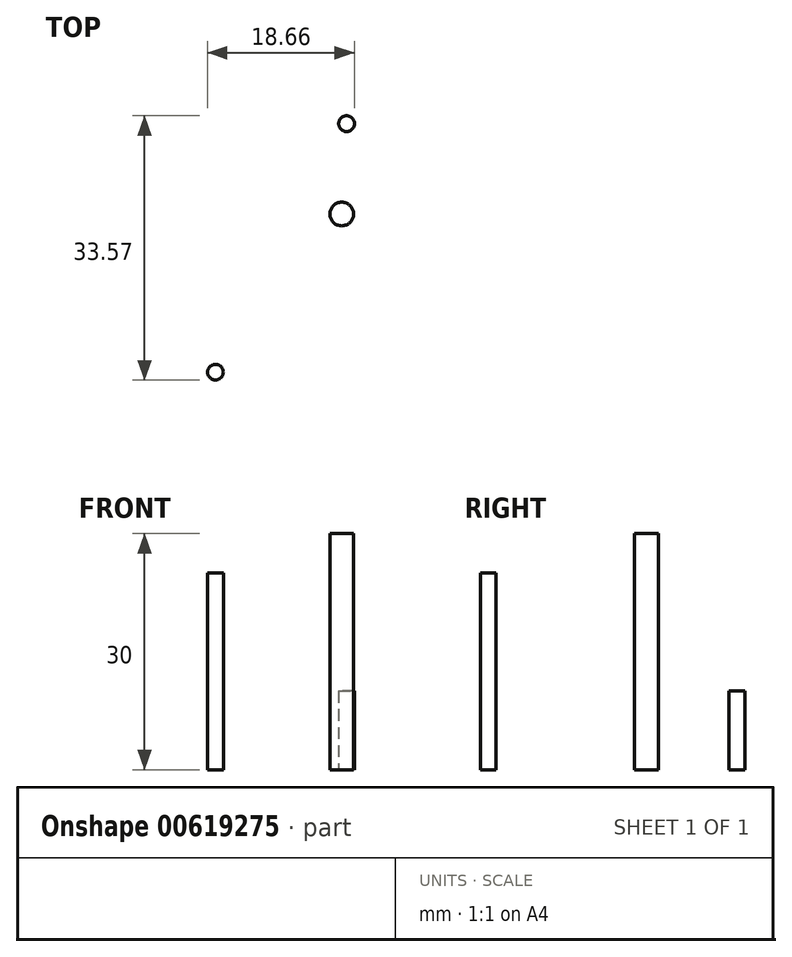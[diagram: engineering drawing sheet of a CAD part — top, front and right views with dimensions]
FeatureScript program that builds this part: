
annotation { "Feature Type Name" : "Feature", "Feature Type Description" : "" }
export const myFeature = defineFeature(function(context is Context, id is Id, definition is map)
    precondition{}
    {
        {
            var Q0;
            Q0=qCreatedBy(makeId("Top.planeOp"),FACE);
            var sketch = newSketch(context, id + "F0", { "sketchPlane" : qUnion([Q0])});
            skCircle(sketch, "E0", {"center": v(26.42, 32.5) * mm, "radius": 1 * mm});
            skSolve(sketch);
        }
        {
            var Q0;
            Q0=makeQuery(id+"F0.imprint","IMPRINT",FACE,{"disambiguationData":[TD([[makeQuery(id+"F0.imprint","IMPRINT",EDGE,{"derivedFrom":sQuery(id+"F0.wireOp",EDGE,"HmnpBGPK-XCcR-qBLW-umx0-wRZoGpGYpxc2")}),1.0]])]});
            var Q1;
            Q1=makeQuery(id+"F0.imprint","IMPRINT",FACE,{"disambiguationData":[TD([[makeQuery(id+"F0.imprint","IMPRINT",EDGE,{"derivedFrom":sQuery(id+"F0.wireOp",EDGE,"E0")}),1.0]])]});
            var Q2;
            Q2=makeQuery(id+"F0.imprint","IMPRINT",FACE,{"disambiguationData":[TD([[makeQuery(id+"F0.imprint","IMPRINT",EDGE,{"derivedFrom":sQuery(id+"F0.wireOp",EDGE,"ZV8fRuly-QuCs-XrdZ-uMXn-ZUZRQThLSaRu")}),-1.0]])]});
            extrude(context, id + "F1", {"entities" : qUnion([Q0, Q1, Q2]), "depth" : 25 * mm, "offsetDistance" : 25 * mm});
        }
        {
            var Q0;
            Q0=qCreatedBy(makeId("Top.planeOp"),FACE);
            var sketch = newSketch(context, id + "F2", { "sketchPlane" : qUnion([Q0])});
            skCircle(sketch, "E1", {"center": v(43.08, 64.08) * mm, "radius": 1 * mm});
            skSolve(sketch);
        }
        {
            var Q0;
            Q0 = qSketchRegion(id + "F2", true);
            extrude(context, id + "F3", {"entities" : qUnion([Q0]), "depth" : 10 * mm, "offsetDistance" : 25 * mm});
        }
        {
            var Q0;
            Q0=qCreatedBy(makeId("Top.planeOp"),FACE);
            var sketch = newSketch(context, id + "F4", { "sketchPlane" : qUnion([Q0])});
            skCircle(sketch, "E2", {"center": v(42.47, 52.6) * mm, "radius": 1.5 * mm});
            skSolve(sketch);
        }
        {
            var Q0;
            Q0=makeQuery(id+"F4.imprint","IMPRINT",FACE,{"disambiguationData":[TD([[makeQuery(id+"F4.imprint","IMPRINT",EDGE,{"derivedFrom":sQuery(id+"F4.wireOp",EDGE,"E2")}),1.0]])]});
            extrude(context, id + "F5", {"entities" : qUnion([Q0]), "depth" : 30 * mm, "offsetDistance" : 25 * mm});
        }
    });
